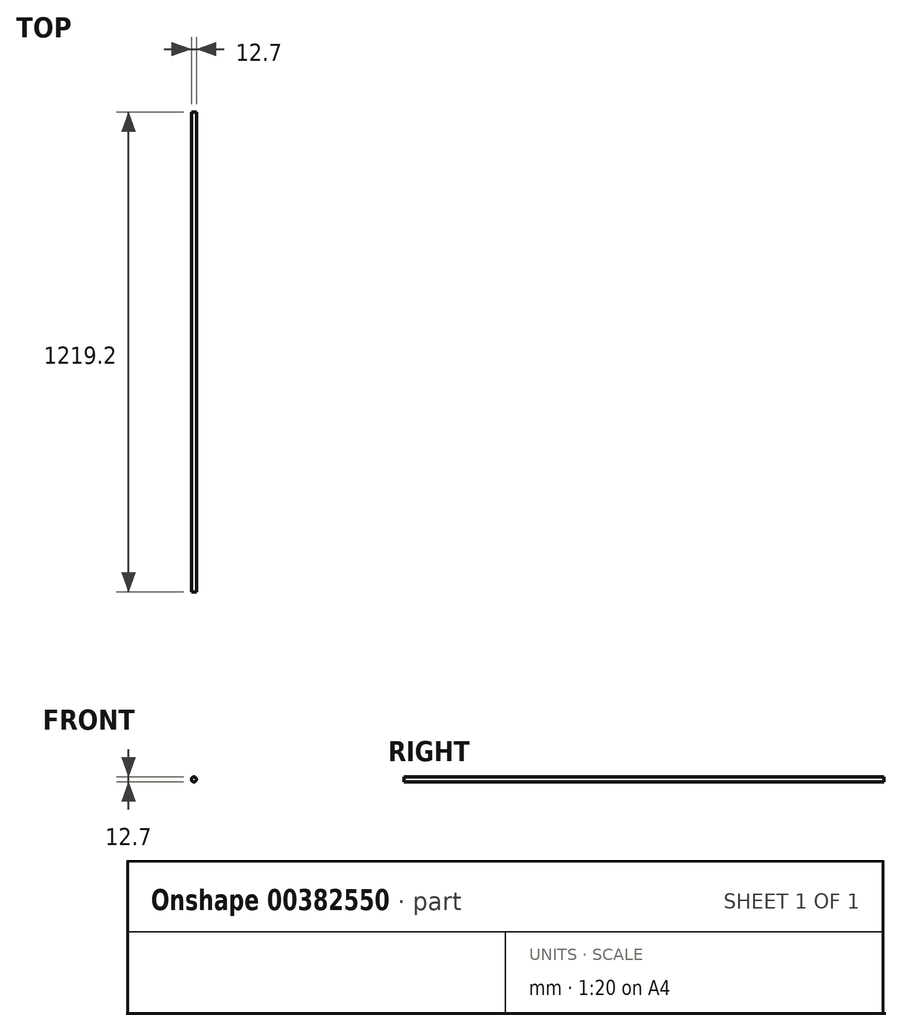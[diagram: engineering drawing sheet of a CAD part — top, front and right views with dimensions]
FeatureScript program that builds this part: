
annotation { "Feature Type Name" : "Feature", "Feature Type Description" : "" }
export const myFeature = defineFeature(function(context is Context, id is Id, definition is map)
    precondition{}
    {
        {
            var Q0;
            Q0=qCreatedBy(makeId("Front.planeOp"),FACE);
            var sketch = newSketch(context, id + "F0", { "sketchPlane" : qUnion([Q0])});
            skCircle(sketch, "E0", {"center": v(0, 0) * mm, "radius": 6.35 * mm});
            skSolve(sketch);
        }
        {
            var Q0;
            Q0=makeQuery(id+"F0.imprint","IMPRINT",FACE,{"disambiguationData":[TD([[makeQuery(id+"F0.imprint","IMPRINT",EDGE,{"derivedFrom":sQuery(id+"F0.wireOp",EDGE,"E0")}),1.0]])]});
            extrude(context, id + "F1", {"entities" : qUnion([Q0]), "depth" : 1219.2 * mm});
        }
    });
